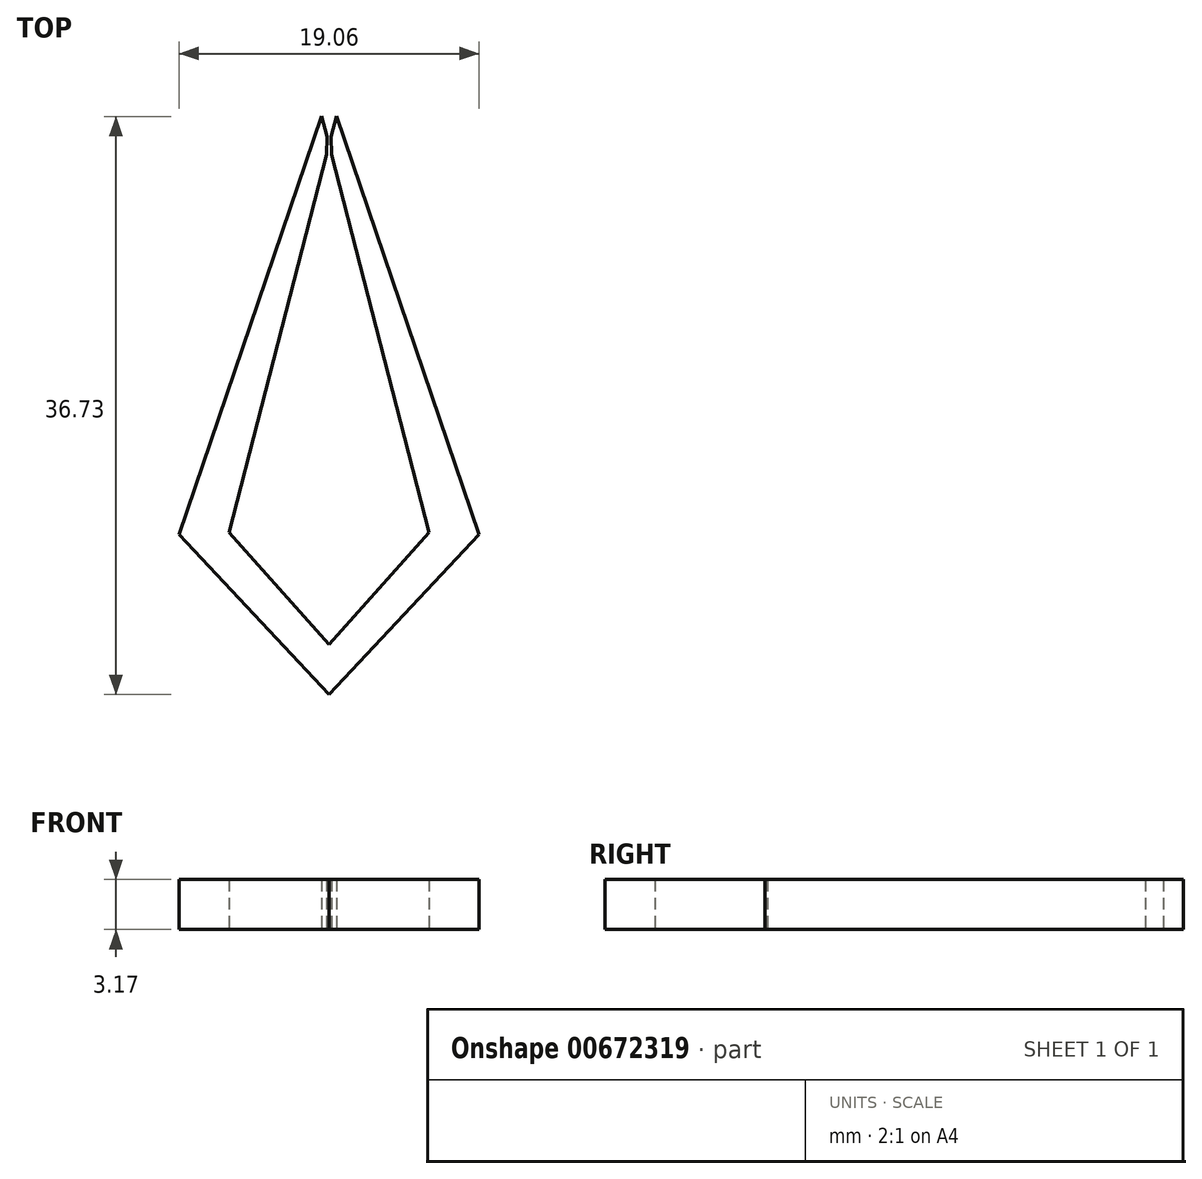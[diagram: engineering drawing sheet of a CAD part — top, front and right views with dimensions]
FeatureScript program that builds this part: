
annotation { "Feature Type Name" : "Feature", "Feature Type Description" : "" }
export const myFeature = defineFeature(function(context is Context, id is Id, definition is map)
    precondition{}
    {
        {
            var Q0;
            Q0=qCreatedBy(makeId("Top.planeOp"),FACE);
            var sketch = newSketch(context, id + "F0", { "sketchPlane" : qUnion([Q0])});
            skLineSegment(sketch, "E0", {"start": v(-0.47, 36.73) * mm, "end": v(-9.53, 10.16) * mm});
            skLineSegment(sketch, "E1", {"start": v(0.47, 36.73) * mm, "end": v(9.53, 10.16) * mm});
            skLineSegment(sketch, "E2", {"start": v(9.53, 10.16) * mm, "end": v(0, 0) * mm});
            skLineSegment(sketch, "E3", {"start": v(-9.53, 10.16) * mm, "end": v(0, 0) * mm});
            skLineSegment(sketch, "E4", {"start": v(-0.16, 34.3) * mm, "end": v(-6.35, 10.31) * mm});
            skLineSegment(sketch, "E5", {"start": v(0.16, 34.3) * mm, "end": v(6.35, 10.31) * mm});
            skLineSegment(sketch, "E6", {"start": v(6.35, 10.31) * mm, "end": v(0, 3.18) * mm});
            skLineSegment(sketch, "E7", {"start": v(-6.35, 10.31) * mm, "end": v(0, 3.18) * mm});
            skLineSegment(sketch, "E8", {"start": v(-0.14, 35.46) * mm, "end": v(-0.47, 36.73) * mm});
            skLineSegment(sketch, "E9.MirrorCS", {"start": v(0.14, 35.46) * mm, "end": v(0.47, 36.73) * mm});
            skPoint(sketch, "E10.orphan", {"position": v(0, 38.1) * mm});
            skLineSegment(sketch, "E11", {"start": v(-0.14, 35.46) * mm, "end": v(-0.16, 34.3) * mm});
            skLineSegment(sketch, "E12.MirrorCS", {"start": v(0.14, 35.46) * mm, "end": v(0.16, 34.3) * mm});
            skPoint(sketch, "E13.orphan", {"position": v(0, 34.93) * mm});
            skSolve(sketch);
        }
        {
            var Q0;
            Q0=makeQuery(id+"F0.imprint","IMPRINT",FACE,{"disambiguationData":[TD([[makeQuery(id+"F0.imprint","IMPRINT",EDGE,{"derivedFrom":sQuery(id+"F0.wireOp",EDGE,"E0")}),1.0]])]});
            extrude(context, id + "F1", {"entities" : qUnion([Q0]), "depth" : 3.17 * mm, "offsetDistance" : 25.4 * mm});
        }
    });
